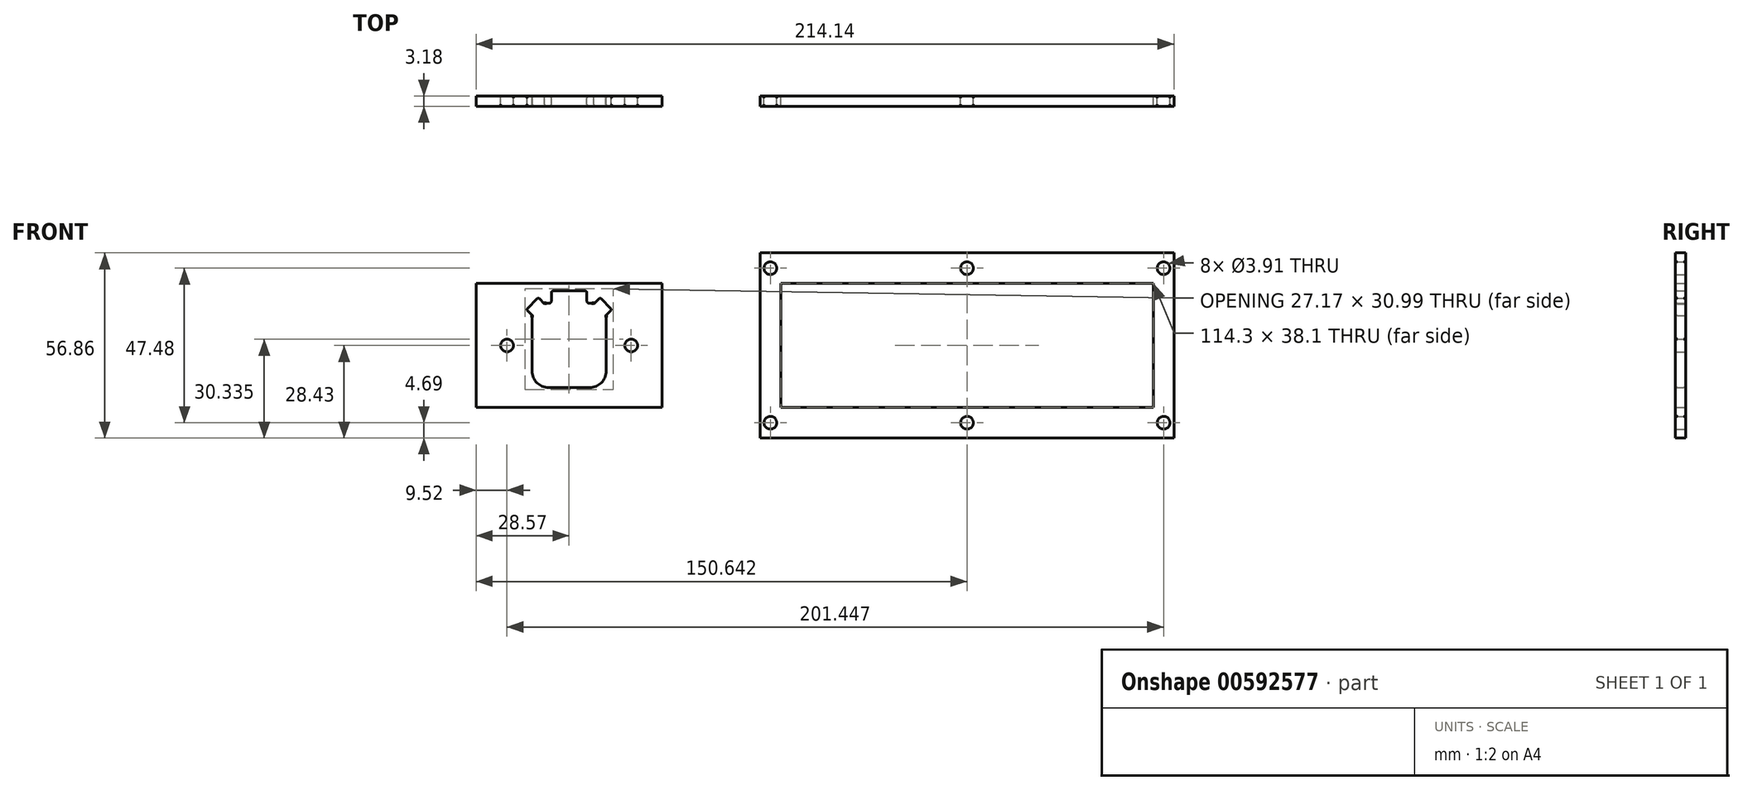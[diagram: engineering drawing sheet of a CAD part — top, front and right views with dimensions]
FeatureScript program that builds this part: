
annotation { "Feature Type Name" : "Feature", "Feature Type Description" : "" }
export const myFeature = defineFeature(function(context is Context, id is Id, definition is map)
    precondition{}
    {
        {
            var Q0;
            Q0=qCreatedBy(makeId("Front.planeOp"),FACE);
            var sketch = newSketch(context, id + "F0", { "sketchPlane" : qUnion([Q0])});
            skLineSegment(sketch, "E0.bottom", {"start": v(-6.29, 11.05) * mm, "end": v(6.29, 11.05) * mm});
            skLineSegment(sketch, "E0.top", {"start": v(-6.29, -11.05) * mm, "end": v(6.29, -11.05) * mm});
            skLineSegment(sketch, "E0.left", {"start": v(-9.46, 7.87) * mm, "end": v(-9.46, -7.87) * mm});
            skLineSegment(sketch, "E0.right", {"start": v(9.46, 7.87) * mm, "end": v(9.46, -7.87) * mm});
            skPoint(sketch, "E0.middle", {"position": v(0, 0) * mm});
            skLineSegment(sketch, "E1", {"start": v(0, 0) * mm, "end": v(0, 11.05) * mm, "construction": true});
            skLineSegment(sketch, "E2", {"start": v(0, 0) * mm, "end": v(-9.46, 0) * mm, "construction": true});
            skLineSegment(sketch, "E3", {"start": v(0, 0) * mm, "end": v(0, -11.05) * mm, "construction": true});
            skLineSegment(sketch, "E4", {"start": v(0, 0) * mm, "end": v(9.46, 0) * mm, "construction": true});
            skLineSegment(sketch, "E5", {"start": v(8.6, -10.05) * mm, "end": v(-8.6, 10.05) * mm, "construction": true});
            skLineSegment(sketch, "E6", {"start": v(8.53, 10.12) * mm, "end": v(-8.53, -10.12) * mm, "construction": true});
            skPoint(sketch, "E7.visualSharp", {"position": v(9.46, 11.05) * mm});
            skArc(sketch, "E7.filletArc", {"start": v(9.46, 7.87) * mm, "mid": v(8.53, 10.12) * mm, "end": v(6.29, 11.05) * mm, "construction": true});
            skPoint(sketch, "E8.visualSharp", {"position": v(-9.46, 11.05) * mm});
            skArc(sketch, "E8.filletArc", {"start": v(-6.29, 11.05) * mm, "mid": v(-8.53, 10.12) * mm, "end": v(-9.46, 7.87) * mm, "construction": true});
            skPoint(sketch, "E9.visualSharp", {"position": v(-9.46, -11.05) * mm});
            skArc(sketch, "E9.filletArc", {"start": v(-9.46, -7.87) * mm, "mid": v(-8.53, -10.12) * mm, "end": v(-6.29, -11.05) * mm});
            skPoint(sketch, "E10.visualSharp", {"position": v(9.46, -11.05) * mm});
            skArc(sketch, "E10.filletArc", {"start": v(6.29, -11.05) * mm, "mid": v(8.53, -10.12) * mm, "end": v(9.46, -7.87) * mm});
            skArc(sketch, "E11", {"start": v(8.04, 10.52) * mm, "mid": v(7.2, 10.91) * mm, "end": v(6.29, 11.05) * mm});
            skArc(sketch, "E12", {"start": v(9.46, 7.87) * mm, "mid": v(9.33, 8.79) * mm, "end": v(8.94, 9.62) * mm});
            skLineSegment(sketch, "E13", {"start": v(-9.47, 11.96) * mm, "end": v(-10.37, 11.06) * mm});
            skArc(sketch, "E14", {"start": v(-6.29, 11.05) * mm, "mid": v(-7.2, 10.91) * mm, "end": v(-8.04, 10.52) * mm});
            skArc(sketch, "E15", {"start": v(-8.94, 9.62) * mm, "mid": v(-9.33, 8.79) * mm, "end": v(-9.46, 7.87) * mm});
            skLineSegment(sketch, "E16", {"start": v(-8.04, 10.52) * mm, "end": v(-8.94, 9.62) * mm, "construction": true});
            skLineSegment(sketch, "E17", {"start": v(6.29, 11.05) * mm, "end": v(8.04, 10.52) * mm, "construction": true});
            skLineSegment(sketch, "E18", {"start": v(9.46, 7.87) * mm, "end": v(8.94, 9.62) * mm, "construction": true});
            skLineSegment(sketch, "E19", {"start": v(-9.46, 7.87) * mm, "end": v(-8.94, 9.62) * mm, "construction": true});
            skLineSegment(sketch, "E20", {"start": v(-8.04, 10.52) * mm, "end": v(-6.29, 11.05) * mm, "construction": true});
            skLineSegment(sketch, "E21", {"start": v(-8.04, 10.52) * mm, "end": v(-9.47, 11.96) * mm});
            skLineSegment(sketch, "E22", {"start": v(-8.94, 9.62) * mm, "end": v(-10.37, 11.06) * mm});
            skLineSegment(sketch, "E23", {"start": v(9.47, 11.96) * mm, "end": v(10.37, 11.06) * mm});
            skLineSegment(sketch, "E24", {"start": v(8.04, 10.52) * mm, "end": v(8.94, 9.62) * mm, "construction": true});
            skLineSegment(sketch, "E25", {"start": v(8.94, 9.62) * mm, "end": v(10.37, 11.06) * mm});
            skLineSegment(sketch, "E26", {"start": v(8.04, 10.52) * mm, "end": v(9.47, 11.96) * mm});
            skLineSegment(sketch, "E27.bottom", {"start": v(-28.58, 19.05) * mm, "end": v(28.57, 19.05) * mm});
            skLineSegment(sketch, "E27.top", {"start": v(-28.57, -19.05) * mm, "end": v(28.58, -19.05) * mm});
            skLineSegment(sketch, "E27.left", {"start": v(-28.58, 19.05) * mm, "end": v(-28.57, -19.05) * mm});
            skLineSegment(sketch, "E27.right", {"start": v(28.57, 19.05) * mm, "end": v(28.58, -19.05) * mm});
            skLineSegment(sketch, "E28", {"start": v(-19.05, 0) * mm, "end": v(19.05, 0) * mm, "construction": true});
            skCircle(sketch, "E29", {"center": v(19.05, 0) * mm, "radius": 1.96 * mm});
            skCircle(sketch, "E30", {"center": v(-19.05, 0) * mm, "radius": 1.96 * mm});
            skCircle(sketch, "E31", {"center": v(19.05, 0) * mm, "radius": 4.45 * mm});
            skCircle(sketch, "E32", {"center": v(-19.05, 0) * mm, "radius": 4.45 * mm});
            skArc(sketch, "E33.0", {"start": v(-6.29, 12.95) * mm, "mid": v(-6.95, 12.91) * mm, "end": v(-7.6, 12.78) * mm});
            skLineSegment(sketch, "E33.1", {"start": v(-7.6, 12.78) * mm, "end": v(-9.27, 14.45) * mm});
            skLineSegment(sketch, "E33.2", {"start": v(-9.67, 14.45) * mm, "end": v(-12.87, 11.26) * mm});
            skLineSegment(sketch, "E33.3", {"start": v(-11.2, 9.19) * mm, "end": v(-12.87, 10.86) * mm});
            skArc(sketch, "E33.4", {"start": v(-11.2, 9.19) * mm, "mid": v(-11.32, 8.54) * mm, "end": v(-11.37, 7.87) * mm});
            skLineSegment(sketch, "E33.5", {"start": v(11.2, 9.19) * mm, "end": v(12.87, 10.86) * mm});
            skLineSegment(sketch, "E33.6", {"start": v(9.67, 14.45) * mm, "end": v(12.87, 11.26) * mm});
            skLineSegment(sketch, "E33.7", {"start": v(7.6, 12.78) * mm, "end": v(9.27, 14.45) * mm});
            skArc(sketch, "E33.8", {"start": v(7.6, 12.78) * mm, "mid": v(6.95, 12.91) * mm, "end": v(6.29, 12.95) * mm});
            skArc(sketch, "E33.9", {"start": v(11.37, 7.87) * mm, "mid": v(11.32, 8.54) * mm, "end": v(11.2, 9.19) * mm});
            skLineSegment(sketch, "E33.10", {"start": v(11.37, 7.87) * mm, "end": v(11.37, -7.87) * mm});
            skArc(sketch, "E33.11", {"start": v(6.29, -12.95) * mm, "mid": v(9.88, -11.47) * mm, "end": v(11.37, -7.87) * mm});
            skLineSegment(sketch, "E33.12", {"start": v(-6.29, -12.95) * mm, "end": v(6.29, -12.95) * mm});
            skArc(sketch, "E33.13", {"start": v(-11.37, -7.87) * mm, "mid": v(-9.88, -11.47) * mm, "end": v(-6.29, -12.95) * mm});
            skLineSegment(sketch, "E33.14", {"start": v(-6.29, 12.95) * mm, "end": v(-6.1, 12.95) * mm});
            skLineSegment(sketch, "E33.15", {"start": v(-11.37, 7.87) * mm, "end": v(-11.37, -7.87) * mm});
            skPoint(sketch, "E34.visualSharp", {"position": v(13.07, 11.06) * mm});
            skArc(sketch, "E34.filletArc", {"start": v(12.87, 10.86) * mm, "mid": v(12.95, 11.06) * mm, "end": v(12.87, 11.26) * mm});
            skPoint(sketch, "E35.visualSharp", {"position": v(9.47, 14.65) * mm});
            skArc(sketch, "E35.filletArc", {"start": v(9.67, 14.45) * mm, "mid": v(9.47, 14.54) * mm, "end": v(9.27, 14.45) * mm});
            skPoint(sketch, "E36.visualSharp", {"position": v(-9.47, 14.65) * mm});
            skArc(sketch, "E36.filletArc", {"start": v(-9.27, 14.45) * mm, "mid": v(-9.47, 14.54) * mm, "end": v(-9.67, 14.45) * mm});
            skPoint(sketch, "E37.visualSharp", {"position": v(-13.07, 11.06) * mm});
            skArc(sketch, "E37.filletArc", {"start": v(-12.87, 11.26) * mm, "mid": v(-12.95, 11.06) * mm, "end": v(-12.87, 10.86) * mm});
            skLineSegment(sketch, "E38.bottom", {"start": v(185.57, 28.43) * mm, "end": v(58.57, 28.43) * mm});
            skLineSegment(sketch, "E38.top", {"start": v(185.57, -28.43) * mm, "end": v(58.57, -28.43) * mm});
            skLineSegment(sketch, "E38.left", {"start": v(185.57, 28.43) * mm, "end": v(185.57, -28.43) * mm});
            skLineSegment(sketch, "E38.right", {"start": v(58.57, 28.43) * mm, "end": v(58.57, -28.43) * mm});
            skPoint(sketch, "E38.middle", {"position": v(122.07, 0) * mm});
            skLineSegment(sketch, "E39.bottom", {"start": v(179.22, 19.05) * mm, "end": v(64.92, 19.05) * mm});
            skLineSegment(sketch, "E39.top", {"start": v(179.22, -19.05) * mm, "end": v(64.92, -19.05) * mm});
            skLineSegment(sketch, "E39.left", {"start": v(179.22, 19.05) * mm, "end": v(179.22, -19.05) * mm});
            skLineSegment(sketch, "E39.right", {"start": v(64.92, 19.05) * mm, "end": v(64.92, -19.05) * mm});
            skCircle(sketch, "E40", {"center": v(61.75, 23.74) * mm, "radius": 1.96 * mm});
            skCircle(sketch, "E41", {"center": v(182.4, 23.74) * mm, "radius": 1.96 * mm});
            skCircle(sketch, "E42", {"center": v(61.75, -23.74) * mm, "radius": 1.96 * mm});
            skCircle(sketch, "E43", {"center": v(182.4, -23.74) * mm, "radius": 1.96 * mm});
            skLineSegment(sketch, "E44.bottom", {"start": v(61.75, 23.74) * mm, "end": v(182.4, 23.74) * mm, "construction": true});
            skLineSegment(sketch, "E44.top", {"start": v(61.75, -23.74) * mm, "end": v(182.4, -23.74) * mm, "construction": true});
            skLineSegment(sketch, "E44.left", {"start": v(61.75, 23.74) * mm, "end": v(61.75, -23.74) * mm, "construction": true});
            skLineSegment(sketch, "E44.right", {"start": v(182.4, 23.74) * mm, "end": v(182.4, -23.74) * mm, "construction": true});
            skLineSegment(sketch, "E45", {"start": v(64.92, 19.05) * mm, "end": v(58.57, 28.43) * mm, "construction": true});
            skCircle(sketch, "E46", {"center": v(122.07, 23.74) * mm, "radius": 1.96 * mm});
            skCircle(sketch, "E47", {"center": v(122.07, -23.74) * mm, "radius": 1.96 * mm});
            skLineSegment(sketch, "E48", {"start": v(0, 12.95) * mm, "end": v(0, 16.76) * mm, "construction": true});
            skLineSegment(sketch, "E49", {"start": v(-4.83, 16.76) * mm, "end": v(4.83, 16.76) * mm});
            skLineSegment(sketch, "E50", {"start": v(-5.46, 16.13) * mm, "end": v(-5.46, 13.59) * mm});
            skLineSegment(sketch, "E51", {"start": v(5.46, 16.13) * mm, "end": v(5.46, 13.59) * mm});
            skPoint(sketch, "E52.visualSharp", {"position": v(-5.46, 16.76) * mm});
            skArc(sketch, "E52.filletArc", {"start": v(-4.83, 16.76) * mm, "mid": v(-5.28, 16.58) * mm, "end": v(-5.46, 16.13) * mm});
            skPoint(sketch, "E53.visualSharp", {"position": v(5.46, 16.76) * mm});
            skArc(sketch, "E53.filletArc", {"start": v(5.46, 16.13) * mm, "mid": v(5.28, 16.58) * mm, "end": v(4.83, 16.76) * mm});
            skLineSegment(sketch, "E54", {"start": v(-5.46, 12.95) * mm, "end": v(5.46, 12.95) * mm, "construction": true});
            skLineSegment(sketch, "E55", {"start": v(6.1, 12.95) * mm, "end": v(6.29, 12.95) * mm});
            skPoint(sketch, "E56.visualSharp", {"position": v(5.46, 12.95) * mm});
            skArc(sketch, "E56.filletArc", {"start": v(5.46, 13.59) * mm, "mid": v(5.65, 13.14) * mm, "end": v(6.1, 12.95) * mm});
            skPoint(sketch, "E57.visualSharp", {"position": v(-5.46, 12.95) * mm});
            skArc(sketch, "E57.filletArc", {"start": v(-6.1, 12.95) * mm, "mid": v(-5.65, 13.14) * mm, "end": v(-5.46, 13.59) * mm});
            skSolve(sketch);
        }
        {
            var Q0;
            Q0=makeQuery(id+"F0.imprint","IMPRINT",FACE,{"disambiguationData":[TD([[makeQuery(id+"F0.imprint","IMPRINT",EDGE,{"derivedFrom":sQuery(id+"F0.wireOp",EDGE,"E29")}),-1.0]])]});
            var Q1;
            Q1=makeQuery(id+"F0.imprint","IMPRINT",FACE,{"disambiguationData":[TD([[makeQuery(id+"F0.imprint","IMPRINT",EDGE,{"derivedFrom":sQuery(id+"F0.wireOp",EDGE,"E27.bottom")}),-1.0]])]});
            var Q2;
            Q2=makeQuery(id+"F0.imprint","IMPRINT",FACE,{"disambiguationData":[TD([[makeQuery(id+"F0.imprint","IMPRINT",EDGE,{"derivedFrom":sQuery(id+"F0.wireOp",EDGE,"E30")}),-1.0]])]});
            var Q3;
            Q3=makeQuery(id+"F0.imprint","IMPRINT",FACE,{"disambiguationData":[TD([[makeQuery(id+"F0.imprint","IMPRINT",EDGE,{"derivedFrom":sQuery(id+"F0.wireOp",EDGE,"E38.bottom")}),1.0]])]});
            extrude(context, id + "F1", {"entities" : qUnion([Q0, Q1, Q2, Q3]), "depth" : 3.17 * mm, "offsetDistance" : 25.4 * mm});
        }
        {
            var Q0;
            Q0=makeQuery(id+"F1.opExtrude","SWEPT_FACE",FACE,{"disambiguationData":[OSD([sQuery(id+"F0.wireOp",EDGE,"E27.right")])]});
            var sketch = newSketch(context, id + "F2", { "sketchPlane" : qUnion([Q0])});
            skLineSegment(sketch, "E58", {"start": v(-1.59, 19.05) * mm, "end": v(-1.59, -19.05) * mm, "construction": true});
            skLineSegment(sketch, "E59", {"start": v(-3.18, 0) * mm, "end": v(-1.59, 0) * mm, "construction": true});
            skSolve(sketch);
        }
        {
            var Q0;
            Q0=makeQuery(id+"F1.opExtrude","CAP_EDGE",EDGE,{"disambiguationData":[OSD([sQuery(id+"F0.wireOp",EDGE,"E33.12")])],"isStart":false});
            var Q1;
            Q1=makeQuery(id+"F1.opExtrude","CAP_EDGE",EDGE,{"disambiguationData":[OSD([sQuery(id+"F0.wireOp",EDGE,"E33.11")])],"isStart":false});
            var Q2;
            Q2=makeQuery(id+"F1.opExtrude","CAP_EDGE",EDGE,{"disambiguationData":[OSD([sQuery(id+"F0.wireOp",EDGE,"E33.10")])],"isStart":false});
            var Q3;
            Q3=makeQuery(id+"F1.opExtrude","CAP_EDGE",EDGE,{"disambiguationData":[OSD([sQuery(id+"F0.wireOp",EDGE,"E33.9")])],"isStart":false});
            var Q4;
            Q4=makeQuery(id+"F1.opExtrude","CAP_EDGE",EDGE,{"disambiguationData":[OSD([sQuery(id+"F0.wireOp",EDGE,"E33.5")])],"isStart":false});
            var Q5;
            Q5=makeQuery(id+"F1.opExtrude","CAP_EDGE",EDGE,{"disambiguationData":[OSD([sQuery(id+"F0.wireOp",EDGE,"E33.6")])],"isStart":false});
            var Q6;
            Q6=makeQuery(id+"F1.opExtrude","CAP_EDGE",EDGE,{"disambiguationData":[OSD([sQuery(id+"F0.wireOp",EDGE,"E35.filletArc")])],"isStart":false});
            var Q7;
            Q7=makeQuery(id+"F1.opExtrude","CAP_EDGE",EDGE,{"disambiguationData":[OSD([sQuery(id+"F0.wireOp",EDGE,"E33.7")])],"isStart":false});
            var Q8;
            Q8=makeQuery(id+"F1.opExtrude","CAP_EDGE",EDGE,{"disambiguationData":[OSD([sQuery(id+"F0.wireOp",EDGE,"E33.8")])],"isStart":false});
            var Q9;
            Q9=makeQuery(id+"F1.opExtrude","CAP_EDGE",EDGE,{"disambiguationData":[OSD([sQuery(id+"F0.wireOp",EDGE,"E33.14")])],"isStart":false});
            var Q10;
            Q10=makeQuery(id+"F1.opExtrude","CAP_EDGE",EDGE,{"disambiguationData":[OSD([sQuery(id+"F0.wireOp",EDGE,"E33.0")])],"isStart":false});
            var Q11;
            Q11=makeQuery(id+"F1.opExtrude","CAP_EDGE",EDGE,{"disambiguationData":[OSD([sQuery(id+"F0.wireOp",EDGE,"E33.1")])],"isStart":false});
            var Q12;
            Q12=makeQuery(id+"F1.opExtrude","CAP_EDGE",EDGE,{"disambiguationData":[OSD([sQuery(id+"F0.wireOp",EDGE,"E36.filletArc")])],"isStart":false});
            var Q13;
            Q13=makeQuery(id+"F1.opExtrude","CAP_EDGE",EDGE,{"disambiguationData":[OSD([sQuery(id+"F0.wireOp",EDGE,"E33.2")])],"isStart":false});
            var Q14;
            Q14=makeQuery(id+"F1.opExtrude","CAP_EDGE",EDGE,{"disambiguationData":[OSD([sQuery(id+"F0.wireOp",EDGE,"E37.filletArc")])],"isStart":false});
            var Q15;
            Q15=makeQuery(id+"F1.opExtrude","CAP_EDGE",EDGE,{"disambiguationData":[OSD([sQuery(id+"F0.wireOp",EDGE,"E33.3")])],"isStart":false});
            var Q16;
            Q16=makeQuery(id+"F1.opExtrude","CAP_EDGE",EDGE,{"disambiguationData":[OSD([sQuery(id+"F0.wireOp",EDGE,"E33.4")])],"isStart":false});
            var Q17;
            Q17=makeQuery(id+"F1.opExtrude","CAP_EDGE",EDGE,{"disambiguationData":[OSD([sQuery(id+"F0.wireOp",EDGE,"E33.15")])],"isStart":false});
            var Q18;
            Q18=makeQuery(id+"F1.opExtrude","CAP_EDGE",EDGE,{"disambiguationData":[OSD([sQuery(id+"F0.wireOp",EDGE,"E33.13")])],"isStart":false});
            var Q19;
            Q19=makeQuery(id+"F1.opExtrude","CAP_EDGE",EDGE,{"disambiguationData":[OSD([sQuery(id+"F0.wireOp",EDGE,"E33.10")])],"isStart":true});
            var Q20;
            Q20=makeQuery(id+"F1.opExtrude","CAP_EDGE",EDGE,{"disambiguationData":[OSD([sQuery(id+"F0.wireOp",EDGE,"E33.9")])],"isStart":true});
            var Q21;
            Q21=makeQuery(id+"F1.opExtrude","CAP_EDGE",EDGE,{"disambiguationData":[OSD([sQuery(id+"F0.wireOp",EDGE,"E33.5")])],"isStart":true});
            var Q22;
            Q22=makeQuery(id+"F1.opExtrude","CAP_EDGE",EDGE,{"disambiguationData":[OSD([sQuery(id+"F0.wireOp",EDGE,"E33.11")])],"isStart":true});
            var Q23;
            Q23=makeQuery(id+"F1.opExtrude","CAP_EDGE",EDGE,{"disambiguationData":[OSD([sQuery(id+"F0.wireOp",EDGE,"E33.3")])],"isStart":true});
            var Q24;
            Q24=makeQuery(id+"F1.opExtrude","CAP_EDGE",EDGE,{"disambiguationData":[OSD([sQuery(id+"F0.wireOp",EDGE,"E33.14")])],"isStart":true});
            var Q25;
            Q25=makeQuery(id+"F1.opExtrude","CAP_EDGE",EDGE,{"disambiguationData":[OSD([sQuery(id+"F0.wireOp",EDGE,"E29")])],"isStart":true});
            var Q26;
            Q26=makeQuery(id+"F1.opExtrude","CAP_EDGE",EDGE,{"disambiguationData":[OSD([sQuery(id+"F0.wireOp",EDGE,"E30")])],"isStart":true});
            var Q27;
            Q27=makeQuery(id+"F1.opExtrude","CAP_EDGE",EDGE,{"disambiguationData":[OSD([sQuery(id+"F0.wireOp",EDGE,"E30")])],"isStart":false});
            var Q28;
            Q28=makeQuery(id+"F1.opExtrude","CAP_EDGE",EDGE,{"disambiguationData":[OSD([sQuery(id+"F0.wireOp",EDGE,"E29")])],"isStart":false});
            fillet(context, id + "F3", {"entities" : qUnion([Q0, Q1, Q2, Q3, Q4, Q5, Q6, Q7, Q8, Q9, Q10, Q11, Q12, Q13, Q14, Q15, Q16, Q17, Q18, Q19, Q20, Q21, Q22, Q23, Q24, Q25, Q26, Q27, Q28]), "radius" : 0.64 * mm, "tangentPropagation" : true, "allowEdgeOverflow" : false});
        }
        {
            var Q0;
            Q0=makeQuery(id+"F1.opExtrude","CAP_EDGE",EDGE,{"disambiguationData":[OSD([sQuery(id+"F0.wireOp",EDGE,"E40")])],"isStart":true});
            var Q1;
            Q1=makeQuery(id+"F1.opExtrude","CAP_EDGE",EDGE,{"disambiguationData":[OSD([sQuery(id+"F0.wireOp",EDGE,"E46")])],"isStart":true});
            var Q2;
            Q2=makeQuery(id+"F1.opExtrude","CAP_EDGE",EDGE,{"disambiguationData":[OSD([sQuery(id+"F0.wireOp",EDGE,"E41")])],"isStart":true});
            var Q3;
            Q3=makeQuery(id+"F1.opExtrude","CAP_EDGE",EDGE,{"disambiguationData":[OSD([sQuery(id+"F0.wireOp",EDGE,"E43")])],"isStart":true});
            var Q4;
            Q4=makeQuery(id+"F1.opExtrude","CAP_EDGE",EDGE,{"disambiguationData":[OSD([sQuery(id+"F0.wireOp",EDGE,"E47")])],"isStart":true});
            var Q5;
            Q5=makeQuery(id+"F1.opExtrude","CAP_EDGE",EDGE,{"disambiguationData":[OSD([sQuery(id+"F0.wireOp",EDGE,"E42")])],"isStart":true});
            var Q6;
            Q6=makeQuery(id+"F1.opExtrude","CAP_EDGE",EDGE,{"disambiguationData":[OSD([sQuery(id+"F0.wireOp",EDGE,"E42")])],"isStart":false});
            var Q7;
            Q7=makeQuery(id+"F1.opExtrude","CAP_EDGE",EDGE,{"disambiguationData":[OSD([sQuery(id+"F0.wireOp",EDGE,"E47")])],"isStart":false});
            var Q8;
            Q8=makeQuery(id+"F1.opExtrude","CAP_EDGE",EDGE,{"disambiguationData":[OSD([sQuery(id+"F0.wireOp",EDGE,"E43")])],"isStart":false});
            var Q9;
            Q9=makeQuery(id+"F1.opExtrude","CAP_EDGE",EDGE,{"disambiguationData":[OSD([sQuery(id+"F0.wireOp",EDGE,"E41")])],"isStart":false});
            var Q10;
            Q10=makeQuery(id+"F1.opExtrude","CAP_EDGE",EDGE,{"disambiguationData":[OSD([sQuery(id+"F0.wireOp",EDGE,"E46")])],"isStart":false});
            var Q11;
            Q11=makeQuery(id+"F1.opExtrude","CAP_EDGE",EDGE,{"disambiguationData":[OSD([sQuery(id+"F0.wireOp",EDGE,"E40")])],"isStart":false});
            fillet(context, id + "F4", {"entities" : qUnion([Q0, Q1, Q2, Q3, Q4, Q5, Q6, Q7, Q8, Q9, Q10, Q11]), "radius" : 0.64 * mm, "tangentPropagation" : true, "allowEdgeOverflow" : false});
        }
    });
